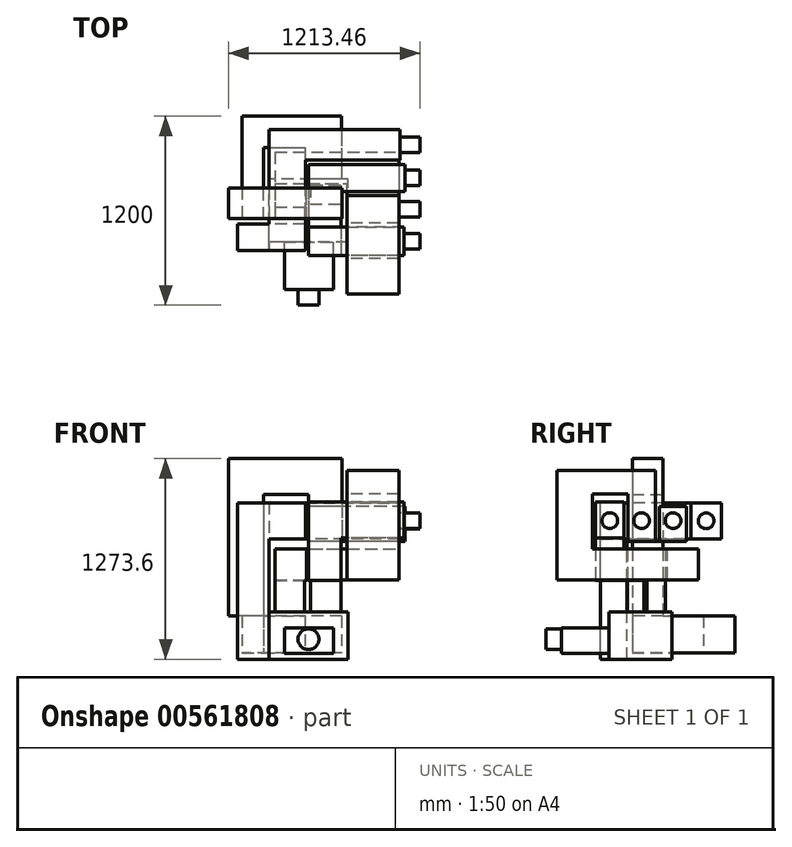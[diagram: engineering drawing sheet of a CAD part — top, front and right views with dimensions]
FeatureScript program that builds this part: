
annotation { "Feature Type Name" : "Feature", "Feature Type Description" : "" }
export const myFeature = defineFeature(function(context is Context, id is Id, definition is map)
    precondition{}
    {
        {
            var Q0;
            Q0=qCreatedBy(makeId("Front.planeOp"),FACE);
            var sketch = newSketch(context, id + "F0", { "sketchPlane" : qUnion([Q0])});
            skLineSegment(sketch, "E0.bottom", {"start": v(250, 100) * mm, "end": v(-250, 100) * mm});
            skLineSegment(sketch, "E0.top", {"start": v(250, -200) * mm, "end": v(-250, -200) * mm});
            skLineSegment(sketch, "E0.left", {"start": v(250, 100) * mm, "end": v(250, -200) * mm});
            skLineSegment(sketch, "E0.right", {"start": v(-250, 100) * mm, "end": v(-250, -200) * mm});
            skSolve(sketch);
        }
        {
            var Q0;
            Q0 = qSketchRegion(id + "F0", true);
            extrude(context, id + "F1", {"entities" : qUnion([Q0]), "depth" : 400 * mm, "offsetDistance" : 25 * mm});
        }
        {
            var Q0;
            Q0=makeQuery(id+"F1.opExtrude","SWEPT_FACE",FACE,{"disambiguationData":[OSD([sQuery(id+"F0.wireOp",EDGE,"E0.bottom")])]});
            var sketch = newSketch(context, id + "F2", { "sketchPlane" : qUnion([Q0])});
            skLineSegment(sketch, "E1.bottom", {"start": v(12.7, -39.9) * mm, "end": v(207.34, -39.9) * mm});
            skLineSegment(sketch, "E1.top", {"start": v(12.7, -156.15) * mm, "end": v(207.34, -156.15) * mm});
            skLineSegment(sketch, "E1.left", {"start": v(12.7, -39.9) * mm, "end": v(12.7, -156.15) * mm});
            skLineSegment(sketch, "E1.right", {"start": v(207.34, -39.9) * mm, "end": v(207.34, -156.15) * mm});
            skLineSegment(sketch, "E2.bottom", {"start": v(-211.35, -175.3) * mm, "end": v(-25.61, -175.3) * mm});
            skLineSegment(sketch, "E2.top", {"start": v(-211.35, -279.98) * mm, "end": v(-25.61, -279.98) * mm});
            skLineSegment(sketch, "E2.left", {"start": v(-211.35, -175.3) * mm, "end": v(-211.35, -279.98) * mm});
            skLineSegment(sketch, "E2.right", {"start": v(-25.61, -175.3) * mm, "end": v(-25.61, -279.98) * mm});
            skSolve(sketch);
        }
        {
            var Q0;
            Q0 = qSketchRegion(id + "F2", true);
            extrude(context, id + "F3", {"entities" : qUnion([Q0]), "operationType" : NewBodyOperationType.ADD, "depth" : 200 * mm, "offsetDistance" : 25 * mm});
        }
        {
            var Q0;
            Q0=makeQuery(id+"F3.opExtrude","CAP_FACE",FACE,{"disambiguationData":[OSD([sQuery(id+"F2.wireOp",EDGE,"E2.bottom"),sQuery(id+"F2.wireOp",EDGE,"E2.top"),sQuery(id+"F2.wireOp",EDGE,"E2.left"),sQuery(id+"F2.wireOp",EDGE,"E2.right")])],"isStart":false});
            var sketch = newSketch(context, id + "F4", { "sketchPlane" : qUnion([Q0])});
            skLineSegment(sketch, "E3.bottom", {"start": v(-211.35, -279.98) * mm, "end": v(-10.91, -279.98) * mm});
            skLineSegment(sketch, "E3.top", {"start": v(-211.35, -28.76) * mm, "end": v(-10.91, -28.76) * mm});
            skLineSegment(sketch, "E3.left", {"start": v(-211.35, -279.98) * mm, "end": v(-211.35, -28.76) * mm});
            skLineSegment(sketch, "E3.right", {"start": v(-10.91, -279.98) * mm, "end": v(-10.91, -28.76) * mm});
            skLineSegment(sketch, "E4.bottom", {"start": v(207.34, -39) * mm, "end": v(0, -39) * mm});
            skLineSegment(sketch, "E4.top", {"start": v(207.34, -283.54) * mm, "end": v(0, -283.54) * mm});
            skLineSegment(sketch, "E4.left", {"start": v(207.34, -39) * mm, "end": v(207.34, -283.54) * mm});
            skLineSegment(sketch, "E4.right", {"start": v(0, -39) * mm, "end": v(0, -283.54) * mm});
            skSolve(sketch);
        }
        {
            var Q0;
            Q0 = qSketchRegion(id + "F4", true);
            extrude(context, id + "F5", {"entities" : qUnion([Q0]), "operationType" : NewBodyOperationType.ADD, "depth" : 200 * mm, "offsetDistance" : 25 * mm});
        }
        {
            var Q0;
            Q0=makeQuery(id+"F1.opExtrude","CAP_FACE",FACE,{"disambiguationData":[OSD([sQuery(id+"F0.wireOp",EDGE,"E0.bottom"),sQuery(id+"F0.wireOp",EDGE,"E0.top"),sQuery(id+"F0.wireOp",EDGE,"E0.left"),sQuery(id+"F0.wireOp",EDGE,"E0.right")])],"isStart":false});
            var sketch = newSketch(context, id + "F6", { "sketchPlane" : qUnion([Q0])});
            skLineSegment(sketch, "E5.bottom", {"start": v(-152.45, 0) * mm, "end": v(158.78, 0) * mm});
            skLineSegment(sketch, "E5.top", {"start": v(-152.45, -161.78) * mm, "end": v(158.78, -161.78) * mm});
            skLineSegment(sketch, "E5.left", {"start": v(-152.45, 0) * mm, "end": v(-152.45, -161.78) * mm});
            skLineSegment(sketch, "E5.right", {"start": v(158.78, 0) * mm, "end": v(158.78, -161.78) * mm});
            skSolve(sketch);
        }
        {
            var Q0;
            Q0 = qSketchRegion(id + "F6", true);
            extrude(context, id + "F7", {"entities" : qUnion([Q0]), "operationType" : NewBodyOperationType.ADD, "depth" : 300 * mm, "offsetDistance" : 25 * mm});
        }
        {
            var Q0;
            Q0=makeQuery(id+"F5.opExtrude","SWEPT_FACE",FACE,{"disambiguationData":[OSD([sQuery(id+"F4.wireOp",EDGE,"E3.top")])]});
            var sketch = newSketch(context, id + "F8", { "sketchPlane" : qUnion([Q0])});
            skLineSegment(sketch, "E6.bottom", {"start": v(211.35, 500) * mm, "end": v(-574.17, 500) * mm});
            skLineSegment(sketch, "E6.top", {"start": v(211.35, 303.72) * mm, "end": v(-574.17, 303.72) * mm});
            skLineSegment(sketch, "E6.left", {"start": v(211.35, 500) * mm, "end": v(211.35, 303.72) * mm});
            skLineSegment(sketch, "E6.right", {"start": v(-574.17, 500) * mm, "end": v(-574.17, 303.72) * mm});
            skSolve(sketch);
        }
        {
            var Q0;
            Q0 = qSketchRegion(id + "F8", true);
            extrude(context, id + "F9", {"entities" : qUnion([Q0]), "operationType" : NewBodyOperationType.ADD, "depth" : 200 * mm, "offsetDistance" : 25 * mm});
        }
        {
            var Q0;
            Q0=makeQuery(id+"F5.opExtrude","SWEPT_FACE",FACE,{"disambiguationData":[OSD([sQuery(id+"F4.wireOp",EDGE,"E4.top")])]});
            extrude(context, id + "F10", {"entities" : qUnion([Q0]), "operationType" : NewBodyOperationType.ADD, "depth" : 200 * mm, "offsetDistance" : 25 * mm});
        }
        {
            var Q0;
            {var subQ0=sQuery(id+"F4.wireOp",EDGE,"E4.top");Q0=makeQuery(id+"F10.boolean.opBoolean","MERGE",FACE,{"derivedFrom":[makeQuery(id+"F5.opExtrude","CAP_FACE",FACE,{"disambiguationData":[OSD([sQuery(id+"F4.wireOp",EDGE,"E4.bottom"),subQ0,sQuery(id+"F4.wireOp",EDGE,"E4.left"),sQuery(id+"F4.wireOp",EDGE,"E4.right")])],"isStart":false}),makeQuery(id+"F10.opExtrude","SWEPT_FACE",FACE,{"disambiguationData":[OSD([subQ0]),TDD([makeQuery(id+"F5.opExtrude","CAP_EDGE",EDGE,{"disambiguationData":[OSD([subQ0])],"isStart":false})])]})]});}
            var sketch = newSketch(context, id + "F11", { "sketchPlane" : qUnion([Q0])});
            skLineSegment(sketch, "E7.bottom", {"start": v(0, -483.54) * mm, "end": v(207.34, -483.54) * mm});
            skLineSegment(sketch, "E7.top", {"start": v(0, -304.74) * mm, "end": v(207.34, -304.74) * mm});
            skLineSegment(sketch, "E7.left", {"start": v(0, -483.54) * mm, "end": v(0, -304.74) * mm});
            skLineSegment(sketch, "E7.right", {"start": v(207.34, -483.54) * mm, "end": v(207.34, -304.74) * mm});
            skSolve(sketch);
        }
        {
            var Q0;
            Q0 = qSketchRegion(id + "F11", true);
            extrude(context, id + "F12", {"entities" : qUnion([Q0]), "operationType" : NewBodyOperationType.ADD, "depth" : 300 * mm, "offsetDistance" : 25 * mm});
        }
        {
            var Q0;
            Q0=makeQuery(id+"F9.opExtrude","CAP_FACE",FACE,{"disambiguationData":[OSD([sQuery(id+"F8.wireOp",EDGE,"E6.bottom"),sQuery(id+"F8.wireOp",EDGE,"E6.top"),sQuery(id+"F8.wireOp",EDGE,"E6.left"),sQuery(id+"F8.wireOp",EDGE,"E6.right")])],"isStart":true});
            var sketch = newSketch(context, id + "F13", { "sketchPlane" : qUnion([Q0])});
            skLineSegment(sketch, "E8.bottom", {"start": v(574.17, 500) * mm, "end": v(243.45, 500) * mm});
            skLineSegment(sketch, "E8.top", {"start": v(574.17, 303.72) * mm, "end": v(243.45, 303.72) * mm});
            skLineSegment(sketch, "E8.left", {"start": v(574.17, 500) * mm, "end": v(574.17, 303.72) * mm});
            skLineSegment(sketch, "E8.right", {"start": v(243.45, 500) * mm, "end": v(243.45, 303.72) * mm});
            skSolve(sketch);
        }
        {
            var Q0;
            Q0 = qSketchRegion(id + "F13", true);
            extrude(context, id + "F14", {"entities" : qUnion([Q0]), "operationType" : NewBodyOperationType.ADD, "depth" : 700 * mm, "offsetDistance" : 25 * mm});
        }
        {
            var Q0;
            {var subQ0=sQuery(id+"F4.wireOp",EDGE,"E4.left");Q0=makeQuery(id+"F12.boolean.opBoolean","MERGE",FACE,{"derivedFrom":[makeQuery(id+"F10.boolean.opBoolean","MERGE",FACE,{"derivedFrom":[makeQuery(id+"F5.boolean.opBoolean","MERGE",FACE,{"derivedFrom":[makeQuery(id+"F3.opExtrude","SWEPT_FACE",FACE,{"disambiguationData":[OSD([sQuery(id+"F2.wireOp",EDGE,"E1.right")])]}),makeQuery(id+"F5.opExtrude","SWEPT_FACE",FACE,{"disambiguationData":[OSD([subQ0])]})]}),makeQuery(id+"F10.opExtrude","SWEPT_FACE",FACE,{"disambiguationData":[OSD([sQuery(id+"F4.wireOp",EDGE,"E4.top"),subQ0])]})]}),makeQuery(id+"F12.opExtrude","SWEPT_FACE",FACE,{"disambiguationData":[OSD([sQuery(id+"F11.wireOp",EDGE,"E7.right")])]})]});}
            var sketch = newSketch(context, id + "F15", { "sketchPlane" : qUnion([Q0])});
            skLineSegment(sketch, "E9.bottom", {"start": v(-304.74, 800) * mm, "end": v(-483.54, 800) * mm});
            skLineSegment(sketch, "E9.top", {"start": v(-304.74, 570.82) * mm, "end": v(-483.54, 570.82) * mm});
            skLineSegment(sketch, "E9.left", {"start": v(-304.74, 800) * mm, "end": v(-304.74, 570.82) * mm});
            skLineSegment(sketch, "E9.right", {"start": v(-483.54, 800) * mm, "end": v(-483.54, 570.82) * mm});
            skSolve(sketch);
        }
        {
            var Q0;
            Q0 = qSketchRegion(id + "F15", true);
            extrude(context, id + "F16", {"entities" : qUnion([Q0]), "operationType" : NewBodyOperationType.ADD, "depth" : 400 * mm, "offsetDistance" : 25 * mm});
        }
        {
            var Q0;
            Q0=makeQuery(id+"F1.opExtrude","SWEPT_FACE",FACE,{"disambiguationData":[OSD([sQuery(id+"F0.wireOp",EDGE,"E0.right")])]});
            var sketch = newSketch(context, id + "F17", { "sketchPlane" : qUnion([Q0])});
            skLineSegment(sketch, "E10.bottom", {"start": v(285.23, -200) * mm, "end": v(451.3, -200) * mm});
            skLineSegment(sketch, "E10.top", {"start": v(285.23, 192.94) * mm, "end": v(451.3, 192.94) * mm});
            skLineSegment(sketch, "E10.left", {"start": v(285.23, -200) * mm, "end": v(285.23, 192.94) * mm});
            skLineSegment(sketch, "E10.right", {"start": v(451.3, -200) * mm, "end": v(451.3, 192.94) * mm});
            skSolve(sketch);
        }
        {
            var Q0;
            Q0 = qSketchRegion(id + "F17", true);
            extrude(context, id + "F18", {"entities" : qUnion([Q0]), "operationType" : NewBodyOperationType.ADD, "depth" : 200 * mm, "offsetDistance" : 25 * mm});
        }
        {
            var Q0;
            Q0=makeQuery(id+"F18.opExtrude","SWEPT_FACE",FACE,{"disambiguationData":[OSD([sQuery(id+"F17.wireOp",EDGE,"E10.top")])]});
            extrude(context, id + "F19", {"entities" : qUnion([Q0]), "operationType" : NewBodyOperationType.ADD, "depth" : 600 * mm, "offsetDistance" : 25 * mm});
        }
        {
            var Q0;
            {var subQ0=sQuery(id+"F17.wireOp",EDGE,"E10.top");Q0=makeQuery(id+"F19.boolean.opBoolean","MERGE",FACE,{"derivedFrom":[makeQuery(id+"F18.opExtrude","CAP_FACE",FACE,{"disambiguationData":[OSD([sQuery(id+"F17.wireOp",EDGE,"E10.bottom"),subQ0,sQuery(id+"F17.wireOp",EDGE,"E10.left"),sQuery(id+"F17.wireOp",EDGE,"E10.right")])],"isStart":true}),makeQuery(id+"F19.opExtrude","SWEPT_FACE",FACE,{"disambiguationData":[OSD([subQ0]),TDD([makeQuery(id+"F18.opExtrude","CAP_EDGE",EDGE,{"disambiguationData":[OSD([subQ0])],"isStart":true})])]})]});}
            var sketch = newSketch(context, id + "F20", { "sketchPlane" : qUnion([Q0])});
            skLineSegment(sketch, "E11.bottom", {"start": v(-451.3, 792.94) * mm, "end": v(-285.23, 792.94) * mm});
            skLineSegment(sketch, "E11.top", {"start": v(-451.3, 564.86) * mm, "end": v(-285.23, 564.86) * mm});
            skLineSegment(sketch, "E11.left", {"start": v(-451.3, 792.94) * mm, "end": v(-451.3, 564.86) * mm});
            skLineSegment(sketch, "E11.right", {"start": v(-285.23, 792.94) * mm, "end": v(-285.23, 564.86) * mm});
            skSolve(sketch);
        }
        {
            var Q0;
            Q0 = qSketchRegion(id + "F20", true);
            extrude(context, id + "F21", {"entities" : qUnion([Q0]), "operationType" : NewBodyOperationType.ADD, "depth" : 230 * mm, "offsetDistance" : 25 * mm});
        }
        {
            var Q0;
            {var subQ0=sQuery(id+"F17.wireOp",EDGE,"E10.left");Q0=makeQuery(id+"F21.boolean.opBoolean","MERGE",FACE,{"derivedFrom":[makeQuery(id+"F19.boolean.opBoolean","MERGE",FACE,{"derivedFrom":[makeQuery(id+"F18.opExtrude","SWEPT_FACE",FACE,{"disambiguationData":[OSD([subQ0])]}),makeQuery(id+"F19.opExtrude","SWEPT_FACE",FACE,{"disambiguationData":[OSD([sQuery(id+"F17.wireOp",EDGE,"E10.top"),subQ0])]})]}),makeQuery(id+"F21.opExtrude","SWEPT_FACE",FACE,{"disambiguationData":[OSD([sQuery(id+"F20.wireOp",EDGE,"E11.right")])]})]});}
            var sketch = newSketch(context, id + "F22", { "sketchPlane" : qUnion([Q0])});
            skLineSegment(sketch, "E12.bottom", {"start": v(20, 792.94) * mm, "end": v(250, 792.94) * mm});
            skLineSegment(sketch, "E12.top", {"start": v(20, 564.86) * mm, "end": v(250, 564.86) * mm});
            skLineSegment(sketch, "E12.left", {"start": v(20, 792.94) * mm, "end": v(20, 564.86) * mm});
            skLineSegment(sketch, "E12.right", {"start": v(250, 792.94) * mm, "end": v(250, 564.86) * mm});
            skSolve(sketch);
        }
        {
            var Q0;
            Q0 = qSketchRegion(id + "F22", true);
            extrude(context, id + "F23", {"entities" : qUnion([Q0]), "operationType" : NewBodyOperationType.ADD, "depth" : 600 * mm, "offsetDistance" : 25 * mm});
        }
        {
            var Q0;
            Q0=makeQuery(id+"F23.boolean.opBoolean","MERGE",FACE,{"derivedFrom":[makeQuery(id+"F21.opExtrude","CAP_FACE",FACE,{"disambiguationData":[OSD([sQuery(id+"F20.wireOp",EDGE,"E11.bottom"),sQuery(id+"F20.wireOp",EDGE,"E11.top"),sQuery(id+"F20.wireOp",EDGE,"E11.left"),sQuery(id+"F20.wireOp",EDGE,"E11.right")])],"isStart":false}),makeQuery(id+"F23.opExtrude","SWEPT_FACE",FACE,{"disambiguationData":[OSD([sQuery(id+"F22.wireOp",EDGE,"E12.left")])]})]});
            var sketch = newSketch(context, id + "F24", { "sketchPlane" : qUnion([Q0])});
            skLineSegment(sketch, "E13.bottom", {"start": v(314.77, 792.94) * mm, "end": v(122.82, 792.94) * mm});
            skLineSegment(sketch, "E13.top", {"start": v(314.77, 564.86) * mm, "end": v(122.82, 564.86) * mm});
            skLineSegment(sketch, "E13.left", {"start": v(314.77, 792.94) * mm, "end": v(314.77, 564.86) * mm});
            skLineSegment(sketch, "E13.right", {"start": v(122.82, 792.94) * mm, "end": v(122.82, 564.86) * mm});
            skSolve(sketch);
        }
        {
            var Q0;
            Q0 = qSketchRegion(id + "F24", true);
            extrude(context, id + "F25", {"entities" : qUnion([Q0]), "operationType" : NewBodyOperationType.ADD, "depth" : 600 * mm, "offsetDistance" : 25 * mm});
        }
        {
            var Q0;
            Q0=makeQuery(id+"F14.boolean.opBoolean","MERGE",FACE,{"derivedFrom":[makeQuery(id+"F9.boolean.opBoolean","MERGE",FACE,{"derivedFrom":[makeQuery(id+"F5.opExtrude","CAP_FACE",FACE,{"disambiguationData":[OSD([sQuery(id+"F4.wireOp",EDGE,"E3.bottom"),sQuery(id+"F4.wireOp",EDGE,"E3.top"),sQuery(id+"F4.wireOp",EDGE,"E3.left"),sQuery(id+"F4.wireOp",EDGE,"E3.right")])],"isStart":false}),makeQuery(id+"F9.opExtrude","SWEPT_FACE",FACE,{"disambiguationData":[OSD([sQuery(id+"F8.wireOp",EDGE,"E6.bottom")])]})]}),makeQuery(id+"F14.opExtrude","SWEPT_FACE",FACE,{"disambiguationData":[OSD([sQuery(id+"F13.wireOp",EDGE,"E8.bottom")])]})]});
            var sketch = newSketch(context, id + "F26", { "sketchPlane" : qUnion([Q0])});
            skLineSegment(sketch, "E14.bottom", {"start": v(243.45, -728.76) * mm, "end": v(574.17, -728.76) * mm});
            skLineSegment(sketch, "E14.top", {"start": v(243.45, -504.32) * mm, "end": v(574.17, -504.32) * mm});
            skLineSegment(sketch, "E14.left", {"start": v(243.45, -728.76) * mm, "end": v(243.45, -504.32) * mm});
            skLineSegment(sketch, "E14.right", {"start": v(574.17, -728.76) * mm, "end": v(574.17, -504.32) * mm});
            skSolve(sketch);
        }
        {
            var Q0;
            Q0 = qSketchRegion(id + "F26", true);
            extrude(context, id + "F27", {"entities" : qUnion([Q0]), "operationType" : NewBodyOperationType.ADD, "depth" : 500 * mm, "offsetDistance" : 25 * mm});
        }
        {
            var Q0;
            Q0=makeQuery(id+"F27.opExtrude","SWEPT_FACE",FACE,{"disambiguationData":[OSD([sQuery(id+"F26.wireOp",EDGE,"E14.top")])]});
            var sketch = newSketch(context, id + "F28", { "sketchPlane" : qUnion([Q0])});
            skLineSegment(sketch, "E15.bottom", {"start": v(-574.17, 1000) * mm, "end": v(-243.45, 1000) * mm});
            skLineSegment(sketch, "E15.top", {"start": v(-574.17, 849.06) * mm, "end": v(-243.45, 849.06) * mm});
            skLineSegment(sketch, "E15.left", {"start": v(-574.17, 1000) * mm, "end": v(-574.17, 849.06) * mm});
            skLineSegment(sketch, "E15.right", {"start": v(-243.45, 1000) * mm, "end": v(-243.45, 849.06) * mm});
            skSolve(sketch);
        }
        {
            var Q0;
            Q0 = qSketchRegion(id + "F28", true);
            extrude(context, id + "F29", {"entities" : qUnion([Q0]), "operationType" : NewBodyOperationType.ADD, "depth" : 400 * mm, "offsetDistance" : 25 * mm});
        }
        {
            var Q0;
            Q0=makeQuery(id+"F29.opExtrude","SWEPT_FACE",FACE,{"disambiguationData":[OSD([sQuery(id+"F28.wireOp",EDGE,"E15.top")])]});
            var sketch = newSketch(context, id + "F30", { "sketchPlane" : qUnion([Q0])});
            skLineSegment(sketch, "E16.bottom", {"start": v(574.17, 104.32) * mm, "end": v(243.45, 104.32) * mm});
            skLineSegment(sketch, "E16.top", {"start": v(574.17, 277.94) * mm, "end": v(243.45, 277.94) * mm});
            skLineSegment(sketch, "E16.left", {"start": v(574.17, 104.32) * mm, "end": v(574.17, 277.94) * mm});
            skLineSegment(sketch, "E16.right", {"start": v(243.45, 104.32) * mm, "end": v(243.45, 277.94) * mm});
            skSolve(sketch);
        }
        {
            var Q0;
            Q0 = qSketchRegion(id + "F30", true);
            extrude(context, id + "F31", {"entities" : qUnion([Q0]), "operationType" : NewBodyOperationType.ADD, "depth" : 300 * mm, "offsetDistance" : 25 * mm});
        }
        {
            var Q0;
            Q0=makeQuery(id+"F1.opExtrude","CAP_FACE",FACE,{"disambiguationData":[OSD([sQuery(id+"F0.wireOp",EDGE,"E0.bottom"),sQuery(id+"F0.wireOp",EDGE,"E0.top"),sQuery(id+"F0.wireOp",EDGE,"E0.left"),sQuery(id+"F0.wireOp",EDGE,"E0.right")])],"isStart":true});
            var sketch = newSketch(context, id + "F32", { "sketchPlane" : qUnion([Q0])});
            skLineSegment(sketch, "E17.bottom", {"start": v(-210.52, 73.6) * mm, "end": v(20.39, 73.6) * mm});
            skLineSegment(sketch, "E17.top", {"start": v(-210.52, -158.73) * mm, "end": v(20.39, -158.73) * mm});
            skLineSegment(sketch, "E17.left", {"start": v(-210.52, 73.6) * mm, "end": v(-210.52, -158.73) * mm});
            skLineSegment(sketch, "E17.right", {"start": v(20.39, 73.6) * mm, "end": v(20.39, -158.73) * mm});
            skSolve(sketch);
        }
        {
            var Q0;
            Q0 = qSketchRegion(id + "F32", true);
            extrude(context, id + "F33", {"entities" : qUnion([Q0]), "operationType" : NewBodyOperationType.ADD, "depth" : 400 * mm, "offsetDistance" : 25 * mm});
        }
        {
            var Q0;
            Q0=makeQuery(id+"F33.opExtrude","SWEPT_FACE",FACE,{"disambiguationData":[OSD([sQuery(id+"F32.wireOp",EDGE,"E17.right")])]});
            var sketch = newSketch(context, id + "F34", { "sketchPlane" : qUnion([Q0])});
            skLineSegment(sketch, "E18.bottom", {"start": v(-400, 73.6) * mm, "end": v(-200, 73.6) * mm});
            skLineSegment(sketch, "E18.top", {"start": v(-400, -158.73) * mm, "end": v(-200, -158.73) * mm});
            skLineSegment(sketch, "E18.left", {"start": v(-400, 73.6) * mm, "end": v(-400, -158.73) * mm});
            skLineSegment(sketch, "E18.right", {"start": v(-200, 73.6) * mm, "end": v(-200, -158.73) * mm});
            skSolve(sketch);
        }
        {
            var Q0;
            Q0 = qSketchRegion(id + "F34", true);
            extrude(context, id + "F35", {"entities" : qUnion([Q0]), "operationType" : NewBodyOperationType.ADD, "depth" : 400 * mm, "offsetDistance" : 25 * mm});
        }
        {
            var Q0;
            Q0=makeQuery(id+"F35.opExtrude","SWEPT_FACE",FACE,{"disambiguationData":[OSD([sQuery(id+"F34.wireOp",EDGE,"E18.right")])]});
            var sketch = newSketch(context, id + "F36", { "sketchPlane" : qUnion([Q0])});
            skLineSegment(sketch, "E19.bottom", {"start": v(-420.39, 73.6) * mm, "end": v(-286.07, 73.6) * mm});
            skLineSegment(sketch, "E19.top", {"start": v(-420.39, -158.73) * mm, "end": v(-286.07, -158.73) * mm});
            skLineSegment(sketch, "E19.left", {"start": v(-420.39, 73.6) * mm, "end": v(-420.39, -158.73) * mm});
            skLineSegment(sketch, "E19.right", {"start": v(-286.07, 73.6) * mm, "end": v(-286.07, -158.73) * mm});
            skSolve(sketch);
        }
        {
            var Q0;
            Q0 = qSketchRegion(id + "F36", true);
            extrude(context, id + "F37", {"entities" : qUnion([Q0]), "operationType" : NewBodyOperationType.ADD, "depth" : 450 * mm, "offsetDistance" : 25 * mm});
        }
        {
            var Q0;
            Q0=makeQuery(id+"F37.boolean.opBoolean","MERGE",FACE,{"derivedFrom":[makeQuery(id+"F35.boolean.opBoolean","MERGE",FACE,{"derivedFrom":[makeQuery(id+"F33.opExtrude","SWEPT_FACE",FACE,{"disambiguationData":[OSD([sQuery(id+"F32.wireOp",EDGE,"E17.bottom")])]}),makeQuery(id+"F35.opExtrude","SWEPT_FACE",FACE,{"disambiguationData":[OSD([sQuery(id+"F34.wireOp",EDGE,"E18.bottom")])]})]}),makeQuery(id+"F37.opExtrude","SWEPT_FACE",FACE,{"disambiguationData":[OSD([sQuery(id+"F36.wireOp",EDGE,"E19.bottom")])]})]});
            var sketch = newSketch(context, id + "F38", { "sketchPlane" : qUnion([Q0])});
            skLineSegment(sketch, "E20.bottom", {"start": v(-286.07, -250) * mm, "end": v(-506.12, -250) * mm});
            skLineSegment(sketch, "E20.top", {"start": v(-286.07, -55.14) * mm, "end": v(-506.12, -55.14) * mm});
            skLineSegment(sketch, "E20.left", {"start": v(-286.07, -250) * mm, "end": v(-286.07, -55.14) * mm});
            skLineSegment(sketch, "E20.right", {"start": v(-506.12, -250) * mm, "end": v(-506.12, -55.14) * mm});
            skSolve(sketch);
        }
        {
            var Q0;
            Q0 = qSketchRegion(id + "F38", true);
            extrude(context, id + "F39", {"entities" : qUnion([Q0]), "operationType" : NewBodyOperationType.ADD, "depth" : 1000 * mm, "offsetDistance" : 25 * mm});
        }
        {
            var Q0;
            Q0=makeQuery(id+"F39.boolean.opBoolean","MERGE",FACE,{"derivedFrom":[makeQuery(id+"F37.opExtrude","SWEPT_FACE",FACE,{"disambiguationData":[OSD([sQuery(id+"F36.wireOp",EDGE,"E19.right")])]}),makeQuery(id+"F39.opExtrude","SWEPT_FACE",FACE,{"disambiguationData":[OSD([sQuery(id+"F38.wireOp",EDGE,"E20.left")])]})]});
            var sketch = newSketch(context, id + "F40", { "sketchPlane" : qUnion([Q0])});
            skLineSegment(sketch, "E21.bottom", {"start": v(-250, 1073.6) * mm, "end": v(-55.14, 1073.6) * mm});
            skLineSegment(sketch, "E21.top", {"start": v(-250, 846.93) * mm, "end": v(-55.14, 846.93) * mm});
            skLineSegment(sketch, "E21.left", {"start": v(-250, 1073.6) * mm, "end": v(-250, 846.93) * mm});
            skLineSegment(sketch, "E21.right", {"start": v(-55.14, 1073.6) * mm, "end": v(-55.14, 846.93) * mm});
            skSolve(sketch);
        }
        {
            var Q0;
            Q0 = qSketchRegion(id + "F40", true);
            extrude(context, id + "F41", {"entities" : qUnion([Q0]), "operationType" : NewBodyOperationType.ADD, "depth" : 500 * mm, "offsetDistance" : 25 * mm});
        }
        {
            var Q0;
            Q0=makeQuery(id+"F41.opExtrude","SWEPT_FACE",FACE,{"disambiguationData":[OSD([sQuery(id+"F40.wireOp",EDGE,"E21.top")])]});
            var sketch = newSketch(context, id + "F42", { "sketchPlane" : qUnion([Q0])});
            skPoint(sketch, "E22.oppositeSnap0", {"position": v(-36.07, 250) * mm});
            skLineSegment(sketch, "E22.bottom", {"start": v(213.93, 55.14) * mm, "end": v(0, 55.14) * mm});
            skLineSegment(sketch, "E22.top", {"start": v(213.93, 250) * mm, "end": v(0, 250) * mm});
            skLineSegment(sketch, "E22.left", {"start": v(213.93, 55.14) * mm, "end": v(213.93, 250) * mm});
            skLineSegment(sketch, "E22.right", {"start": v(0, 55.14) * mm, "end": v(0, 250) * mm});
            skSolve(sketch);
        }
        {
            var Q0;
            Q0 = qSketchRegion(id + "F42", true);
            extrude(context, id + "F43", {"entities" : qUnion([Q0]), "operationType" : NewBodyOperationType.ADD, "depth" : 300 * mm, "offsetDistance" : 25 * mm});
        }
        {
            var Q0;
            Q0=makeQuery(id+"F43.boolean.opBoolean","MERGE",FACE,{"derivedFrom":[makeQuery(id+"F41.boolean.opBoolean","MERGE",FACE,{"derivedFrom":[makeQuery(id+"F39.opExtrude","SWEPT_FACE",FACE,{"disambiguationData":[OSD([sQuery(id+"F38.wireOp",EDGE,"E20.top")])]}),makeQuery(id+"F41.opExtrude","SWEPT_FACE",FACE,{"disambiguationData":[OSD([sQuery(id+"F40.wireOp",EDGE,"E21.right")])]})]}),makeQuery(id+"F43.opExtrude","SWEPT_FACE",FACE,{"disambiguationData":[OSD([sQuery(id+"F42.wireOp",EDGE,"E22.bottom")])]})]});
            var sketch = newSketch(context, id + "F44", { "sketchPlane" : qUnion([Q0])});
            skLineSegment(sketch, "E23.bottom", {"start": v(-213.93, 546.93) * mm, "end": v(0, 546.93) * mm});
            skLineSegment(sketch, "E23.top", {"start": v(-213.93, 771.56) * mm, "end": v(0, 771.56) * mm});
            skLineSegment(sketch, "E23.left", {"start": v(-213.93, 546.93) * mm, "end": v(-213.93, 771.56) * mm});
            skLineSegment(sketch, "E23.right", {"start": v(0, 546.93) * mm, "end": v(0, 771.56) * mm});
            skSolve(sketch);
        }
        {
            var Q0;
            Q0 = qSketchRegion(id + "F44", true);
            extrude(context, id + "F45", {"entities" : qUnion([Q0]), "operationType" : NewBodyOperationType.ADD, "depth" : 150 * mm, "offsetDistance" : 25 * mm});
        }
        {
            var Q0;
            Q0=makeQuery(id+"F45.boolean.opBoolean","MERGE",FACE,{"derivedFrom":[makeQuery(id+"F43.boolean.opBoolean","MERGE",FACE,{"derivedFrom":[makeQuery(id+"F41.opExtrude","CAP_FACE",FACE,{"disambiguationData":[OSD([sQuery(id+"F40.wireOp",EDGE,"E21.bottom"),sQuery(id+"F40.wireOp",EDGE,"E21.top"),sQuery(id+"F40.wireOp",EDGE,"E21.left"),sQuery(id+"F40.wireOp",EDGE,"E21.right")])],"isStart":false}),makeQuery(id+"F43.opExtrude","SWEPT_FACE",FACE,{"disambiguationData":[OSD([sQuery(id+"F42.wireOp",EDGE,"E22.left")])]})]}),makeQuery(id+"F45.opExtrude","SWEPT_FACE",FACE,{"disambiguationData":[OSD([sQuery(id+"F44.wireOp",EDGE,"E23.left")])]})]});
            var sketch = newSketch(context, id + "F46", { "sketchPlane" : qUnion([Q0])});
            skLineSegment(sketch, "E24.bottom", {"start": v(94.86, 771.56) * mm, "end": v(-77.57, 771.56) * mm});
            skLineSegment(sketch, "E24.top", {"start": v(94.86, 546.93) * mm, "end": v(-77.57, 546.93) * mm});
            skLineSegment(sketch, "E24.left", {"start": v(94.86, 771.56) * mm, "end": v(94.86, 546.93) * mm});
            skLineSegment(sketch, "E24.right", {"start": v(-77.57, 771.56) * mm, "end": v(-77.57, 546.93) * mm});
            skSolve(sketch);
        }
        {
            var Q0;
            Q0 = qSketchRegion(id + "F46", true);
            extrude(context, id + "F47", {"entities" : qUnion([Q0]), "operationType" : NewBodyOperationType.ADD, "depth" : 400 * mm, "offsetDistance" : 25 * mm});
        }
        {
            var Q0;
            Q0=makeQuery(id+"F7.opExtrude","CAP_FACE",FACE,{"disambiguationData":[OSD([sQuery(id+"F6.wireOp",EDGE,"E5.bottom"),sQuery(id+"F6.wireOp",EDGE,"E5.top"),sQuery(id+"F6.wireOp",EDGE,"E5.left"),sQuery(id+"F6.wireOp",EDGE,"E5.right")])],"isStart":false});
            var sketch = newSketch(context, id + "F48", { "sketchPlane" : qUnion([Q0])});
            skCircle(sketch, "E25", {"center": v(0, -72.73) * mm, "radius": 65.98 * mm});
            skSolve(sketch);
        }
        {
            var Q0;
            Q0 = qSketchRegion(id + "F48", true);
            extrude(context, id + "F49", {"entities" : qUnion([Q0]), "operationType" : NewBodyOperationType.ADD, "depth" : 100 * mm, "offsetDistance" : 25 * mm});
        }
        {
            var Q0;
            Q0=makeQuery(id+"F16.opExtrude","CAP_FACE",FACE,{"disambiguationData":[OSD([sQuery(id+"F15.wireOp",EDGE,"E9.bottom"),sQuery(id+"F15.wireOp",EDGE,"E9.top"),sQuery(id+"F15.wireOp",EDGE,"E9.left"),sQuery(id+"F15.wireOp",EDGE,"E9.right")])],"isStart":false});
            var sketch = newSketch(context, id + "F50", { "sketchPlane" : qUnion([Q0])});
            skCircle(sketch, "E26", {"center": v(-393.54, 680) * mm, "radius": 50 * mm});
            skSolve(sketch);
        }
        {
            var Q0;
            Q0=makeQuery(id+"F50.imprint","IMPRINT",FACE,{"disambiguationData":[TD([[makeQuery(id+"F50.imprint","IMPRINT",EDGE,{"derivedFrom":sQuery(id+"F50.wireOp",EDGE,"E26")}),1.0]])]});
            var Q1;
            Q1=sQuery(id+"F50.wireOp",EDGE,"E26");
            extrude(context, id + "F51", {"entities" : qUnion([Q0]), "operationType" : NewBodyOperationType.ADD, "surfaceEntities" : qUnion([Q1]), "depth" : 100 * mm, "offsetDistance" : 25 * mm});
        }
        {
            var Q0;
            Q0=makeQuery(id+"F31.boolean.opBoolean","MERGE",FACE,{"derivedFrom":[makeQuery(id+"F29.boolean.opBoolean","MERGE",FACE,{"derivedFrom":[makeQuery(id+"F27.boolean.opBoolean","MERGE",FACE,{"derivedFrom":[makeQuery(id+"F14.boolean.opBoolean","MERGE",FACE,{"derivedFrom":[makeQuery(id+"F9.opExtrude","SWEPT_FACE",FACE,{"disambiguationData":[OSD([sQuery(id+"F8.wireOp",EDGE,"E6.right")])]}),makeQuery(id+"F14.opExtrude","SWEPT_FACE",FACE,{"disambiguationData":[OSD([sQuery(id+"F13.wireOp",EDGE,"E8.left")])]})]}),makeQuery(id+"F27.opExtrude","SWEPT_FACE",FACE,{"disambiguationData":[OSD([sQuery(id+"F26.wireOp",EDGE,"E14.right")])]})]}),makeQuery(id+"F29.opExtrude","SWEPT_FACE",FACE,{"disambiguationData":[OSD([sQuery(id+"F28.wireOp",EDGE,"E15.left")])]})]}),makeQuery(id+"F31.opExtrude","SWEPT_FACE",FACE,{"disambiguationData":[OSD([sQuery(id+"F30.wireOp",EDGE,"E16.left")])]})]});
            var sketch = newSketch(context, id + "F52", { "sketchPlane" : qUnion([Q0])});
            skCircle(sketch, "E27", {"center": v(-191.13, 680) * mm, "radius": 50 * mm});
            skSolve(sketch);
        }
        {
            var Q0;
            Q0 = qSketchRegion(id + "F52", true);
            extrude(context, id + "F53", {"entities" : qUnion([Q0]), "operationType" : NewBodyOperationType.ADD, "depth" : 200 * mm, "offsetDistance" : 25 * mm});
        }
        {
            var Q0;
            Q0=makeQuery(id+"F47.opExtrude","CAP_FACE",FACE,{"disambiguationData":[OSD([sQuery(id+"F46.wireOp",EDGE,"E24.bottom"),sQuery(id+"F46.wireOp",EDGE,"E24.top"),sQuery(id+"F46.wireOp",EDGE,"E24.left"),sQuery(id+"F46.wireOp",EDGE,"E24.right")])],"isStart":false});
            var sketch = newSketch(context, id + "F54", { "sketchPlane" : qUnion([Q0])});
            skCircle(sketch, "E28", {"center": v(8.65, 680) * mm, "radius": 50 * mm});
            skSolve(sketch);
        }
        {
            var Q0;
            Q0=makeQuery(id+"F54.imprint","IMPRINT",FACE,{"disambiguationData":[TD([[makeQuery(id+"F54.imprint","IMPRINT",EDGE,{"derivedFrom":sQuery(id+"F54.wireOp",EDGE,"E28")}),1.0]])]});
            extrude(context, id + "F55", {"entities" : qUnion([Q0]), "operationType" : NewBodyOperationType.ADD, "depth" : 200 * mm, "offsetDistance" : 25 * mm});
        }
        {
            var Q0;
            Q0=makeQuery(id+"F25.opExtrude","CAP_FACE",FACE,{"disambiguationData":[OSD([sQuery(id+"F24.wireOp",EDGE,"E13.bottom"),sQuery(id+"F24.wireOp",EDGE,"E13.top"),sQuery(id+"F24.wireOp",EDGE,"E13.left"),sQuery(id+"F24.wireOp",EDGE,"E13.right")])],"isStart":false});
            var sketch = newSketch(context, id + "F56", { "sketchPlane" : qUnion([Q0])});
            skCircle(sketch, "E29", {"center": v(218.8, 678.9) * mm, "radius": 50 * mm});
            skPoint(sketch, "E29.centerSnap0", {"position": v(218.8, 564.86) * mm});
            skPoint(sketch, "E29.centerSnap1", {"position": v(122.82, 678.9) * mm});
            skSolve(sketch);
        }
        {
            var Q0;
            Q0=makeQuery(id+"F56.imprint","IMPRINT",FACE,{"disambiguationData":[TD([[makeQuery(id+"F56.imprint","IMPRINT",EDGE,{"derivedFrom":sQuery(id+"F56.wireOp",EDGE,"E29")}),1.0]])]});
            extrude(context, id + "F57", {"entities" : qUnion([Q0]), "operationType" : NewBodyOperationType.ADD, "depth" : 200 * mm, "offsetDistance" : 25 * mm});
        }
        {
            var Q0;
            Q0=makeQuery(id+"F51.opExtrude","CAP_FACE",FACE,{"disambiguationData":[OSD([sQuery(id+"F50.wireOp",EDGE,"E26")])],"isStart":false});
            var sketch = newSketch(context, id + "F58", { "sketchPlane" : qUnion([Q0])});
            skLineSegment(sketch, "E30.bottom", {"start": v(-758.2, 926.18) * mm, "end": v(635.04, 926.18) * mm});
            skLineSegment(sketch, "E30.top", {"start": v(-758.2, 414.86) * mm, "end": v(635.04, 414.86) * mm});
            skLineSegment(sketch, "E30.left", {"start": v(-758.2, 926.18) * mm, "end": v(-758.2, 414.86) * mm});
            skLineSegment(sketch, "E30.right", {"start": v(635.04, 926.18) * mm, "end": v(635.04, 414.86) * mm});
            skSolve(sketch);
        }
        {
            var Q0;
            Q0=makeQuery(id+"F58.imprint","IMPRINT",FACE,{"disambiguationData":[TD([[makeQuery(id+"F58.imprint","IMPRINT",EDGE,{"derivedFrom":sQuery(id+"F58.wireOp",EDGE,"E30.bottom")}),-1.0]])]});
            extrude(context, id + "F59", {"entities" : qUnion([Q0]), "operationType" : NewBodyOperationType.REMOVE, "depth" : 200 * mm, "offsetDistance" : 25 * mm});
        }
    });
